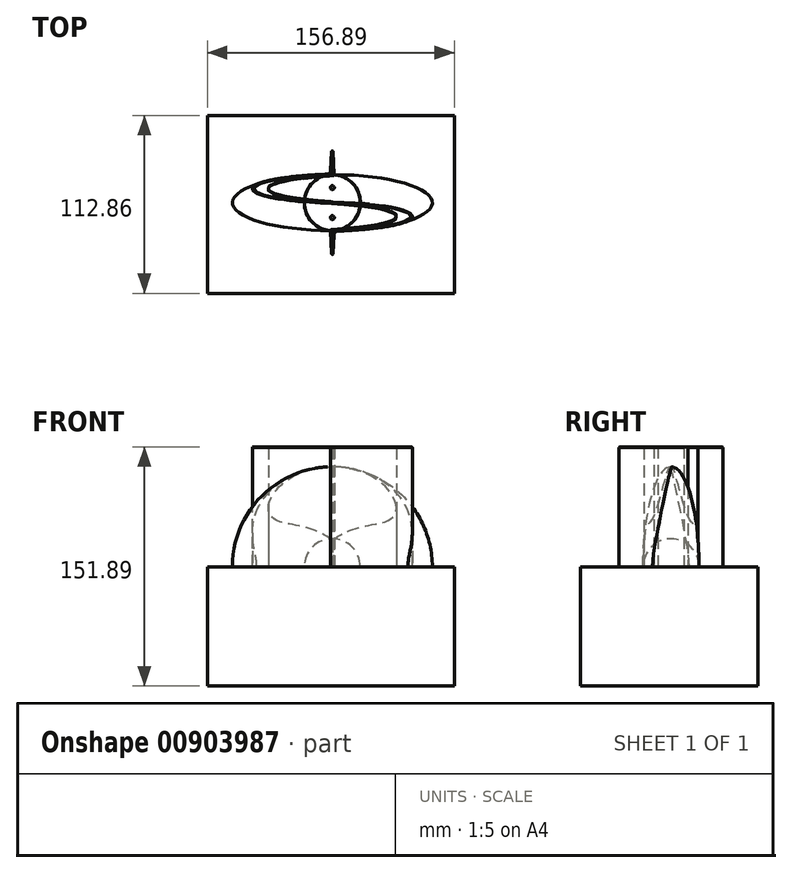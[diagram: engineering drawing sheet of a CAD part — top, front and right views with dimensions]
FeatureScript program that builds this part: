
annotation { "Feature Type Name" : "Feature", "Feature Type Description" : "" }
export const myFeature = defineFeature(function(context is Context, id is Id, definition is map)
    precondition{}
    {
        {
            var Q0;
            Q0=qCreatedBy(makeId("Top.planeOp"),FACE);
            var sketch = newSketch(context, id + "F0", { "sketchPlane" : qUnion([Q0])});
            skEllipticalArc(sketch, "E0", {});
            skEllipticalArc(sketch, "E1", {});
            skLineSegment(sketch, "E2", {"start": v(0, 0.5) * mm, "end": v(0, -0.5) * mm});
            skLineSegment(sketch, "E3", {"start": v(0, 18.17) * mm, "end": v(0, 17.17) * mm});
            const initialGuessF0  = {"E0": [0.0127, 0.008834129127051515, -1, 0, 0.0635, 0.009525, 4.9137469011750206, 1.369438406004566], "E1": [0.0381, 0.008834129127051515, -1, 0, 0.07874, 0.009525, 5.217461570130556, 1.0657237370490302]};
            skSetInitialGuess(sketch, initialGuessF0);
            skSolve(sketch);
        }
        {
            var Q0;
            Q0=qCreatedBy(makeId("Top.planeOp"),FACE);
            var sketch = newSketch(context, id + "F1", { "sketchPlane" : qUnion([Q0])});
            skLineSegment(sketch, "E4", {"start": v(-1.27, 17.17) * mm, "end": v(1.27, 17.17) * mm});
            skLineSegment(sketch, "E5", {"start": v(1.27, 17.17) * mm, "end": v(0, 42.57) * mm});
            skLineSegment(sketch, "E6", {"start": v(0, 42.57) * mm, "end": v(-1.27, 17.17) * mm});
            skSolve(sketch);
        }
        {
            var Q0;
            Q0=makeQuery(id+"F0.imprint","IMPRINT",FACE,{"disambiguationData":[TD([[makeQuery(id+"F0.imprint","IMPRINT",EDGE,{"derivedFrom":sQuery(id+"F0.wireOp",EDGE,"E0")}),1.0]])]});
            var Q1;
            Q1=makeQuery(id+"F1.imprint","IMPRINT",FACE,{"disambiguationData":[TD([[makeQuery(id+"F1.imprint","IMPRINT",EDGE,{"derivedFrom":sQuery(id+"F1.wireOp",EDGE,"E4")}),1.0]])]});
            extrude(context, id + "F2", {"entities" : qUnion([Q0, Q1]), "depth" : 76.2 * mm, "offsetDistance" : 25.4 * mm});
        }
        {
            var Q0;
            Q0=qCreatedBy(makeId("Front.planeOp"),FACE);
            var sketch = newSketch(context, id + "F3", { "sketchPlane" : qUnion([Q0])});
            skLineSegment(sketch, "E7", {"start": v(0, 85.95) * mm, "end": v(0, -92.06) * mm});
            skSolve(sketch);
        }
        {
            var Q0;
            Q0=makeQuery(id+"F2.opExtrude","SWEPT_BODY",BODY,{"disambiguationData":[OSD([sQuery(id+"F1.wireOp",EDGE,"E4"),sQuery(id+"F1.wireOp",EDGE,"E5"),sQuery(id+"F1.wireOp",EDGE,"E6")])]});
            var Q1;
            Q1=makeQuery(id+"F2.opExtrude","SWEPT_BODY",BODY,{"disambiguationData":[OSD([sQuery(id+"F0.wireOp",EDGE,"E0"),sQuery(id+"F0.wireOp",EDGE,"E1"),sQuery(id+"F0.wireOp",EDGE,"E2"),sQuery(id+"F0.wireOp",EDGE,"E3")])]});
            var Q2;
            Q2=sQuery(id+"F3.wireOp",EDGE,"E7");
            circularPattern(context, id + "F4", {"entities" : qUnion([Q0, Q1]), "axis" : qUnion([Q2]), "angle" : 360 * degree, "instanceCount" : 2, "equalSpace" : true});
        }
        {
            var Q0;
            Q0=makeQuery(id+"F2.opExtrude","SWEPT_BODY",BODY,{"disambiguationData":[OSD([sQuery(id+"F0.wireOp",EDGE,"E0"),sQuery(id+"F0.wireOp",EDGE,"E1"),sQuery(id+"F0.wireOp",EDGE,"E2"),sQuery(id+"F0.wireOp",EDGE,"E3")])]});
            var Q1;
            Q1=makeQuery(id+"F2.opExtrude","SWEPT_BODY",BODY,{"disambiguationData":[OSD([sQuery(id+"F1.wireOp",EDGE,"E4"),sQuery(id+"F1.wireOp",EDGE,"E5"),sQuery(id+"F1.wireOp",EDGE,"E6")])]});
            var Q2;
            Q2=makeQuery(id+"F4.opPattern","COPY",BODY,{"derivedFrom":makeQuery(id+"F2.opExtrude","SWEPT_BODY",BODY,{"disambiguationData":[OSD([sQuery(id+"F0.wireOp",EDGE,"E0"),sQuery(id+"F0.wireOp",EDGE,"E1"),sQuery(id+"F0.wireOp",EDGE,"E2"),sQuery(id+"F0.wireOp",EDGE,"E3")])]}),"instanceName":"1"});
            var Q3;
            Q3=makeQuery(id+"F4.opPattern","COPY",BODY,{"derivedFrom":makeQuery(id+"F2.opExtrude","SWEPT_BODY",BODY,{"disambiguationData":[OSD([sQuery(id+"F1.wireOp",EDGE,"E4"),sQuery(id+"F1.wireOp",EDGE,"E5"),sQuery(id+"F1.wireOp",EDGE,"E6")])]}),"instanceName":"1"});
            booleanBodies(context, id + "F5", {"operationType" : BooleanOperationType.UNION, "tools" : qUnion([Q0, Q1, Q2, Q3])});
        }
        {
            var Q0;
            Q0=makeQuery(id+"F2.opExtrude","SWEPT_EDGE",EDGE,{"disambiguationData":[OSD([sQuery(id+"F1.wireOp",EDGE,"E4"),sQuery(id+"F1.wireOp",EDGE,"E5")])]});
            var Q1;
            Q1=makeQuery(id+"F4.opPattern","COPY",EDGE,{"derivedFrom":makeQuery(id+"F2.opExtrude","SWEPT_EDGE",EDGE,{"disambiguationData":[OSD([sQuery(id+"F1.wireOp",EDGE,"E4"),sQuery(id+"F1.wireOp",EDGE,"E5")])]}),"instanceName":"1"});
            fillet(context, id + "F6", {"entities" : qUnion([Q0, Q1]), "radius" : 0.76 * mm, "tangentPropagation" : true, "allowEdgeOverflow" : false});
        }
        {
            var Q0;
            Q0=makeQuery(id+"F5.opBoolean","INTERSECT",EDGE,{"derivedFrom":[makeQuery(id+"F2.opExtrude","SWEPT_FACE",FACE,{"disambiguationData":[OSD([sQuery(id+"F0.wireOp",EDGE,"E0")])]}),makeQuery(id+"F2.opExtrude","SWEPT_FACE",FACE,{"disambiguationData":[OSD([sQuery(id+"F1.wireOp",EDGE,"E6")])]})]});
            var Q1;
            Q1=makeQuery(id+"F5.opBoolean","INTERSECT",EDGE,{"derivedFrom":[makeQuery(id+"F4.opPattern","COPY",FACE,{"derivedFrom":makeQuery(id+"F2.opExtrude","SWEPT_FACE",FACE,{"disambiguationData":[OSD([sQuery(id+"F0.wireOp",EDGE,"E0")])]}),"instanceName":"1"}),makeQuery(id+"F4.opPattern","COPY",FACE,{"derivedFrom":makeQuery(id+"F2.opExtrude","SWEPT_FACE",FACE,{"disambiguationData":[OSD([sQuery(id+"F1.wireOp",EDGE,"E6")])]}),"instanceName":"1"})]});
            fillet(context, id + "F7", {"entities" : qUnion([Q0, Q1]), "radius" : 2.54 * mm, "tangentPropagation" : true, "allowEdgeOverflow" : false});
        }
        {
            var Q0;
            Q0=makeQuery(id+"F2.opExtrude","SWEPT_EDGE",EDGE,{"disambiguationData":[OSD([sQuery(id+"F1.wireOp",EDGE,"E5"),sQuery(id+"F1.wireOp",EDGE,"E6")])]});
            var Q1;
            Q1=makeQuery(id+"F4.opPattern","COPY",EDGE,{"derivedFrom":makeQuery(id+"F2.opExtrude","SWEPT_EDGE",EDGE,{"disambiguationData":[OSD([sQuery(id+"F1.wireOp",EDGE,"E5"),sQuery(id+"F1.wireOp",EDGE,"E6")])]}),"instanceName":"1"});
            fillet(context, id + "F8", {"entities" : qUnion([Q0, Q1]), "radius" : 0.5 * mm, "tangentPropagation" : true, "allowEdgeOverflow" : false});
        }
        {
            var Q0;
            {var subQ0=sQuery(id+"F0.wireOp",EDGE,"E2");Q0=makeQuery(id+"F5.opBoolean","MERGE",EDGE,{"derivedFrom":[makeQuery(id+"F2.opExtrude","SWEPT_EDGE",EDGE,{"disambiguationData":[OSD([sQuery(id+"F0.wireOp",EDGE,"E1"),subQ0])]}),makeQuery(id+"F4.opPattern","COPY",EDGE,{"derivedFrom":makeQuery(id+"F2.opExtrude","SWEPT_EDGE",EDGE,{"disambiguationData":[OSD([sQuery(id+"F0.wireOp",EDGE,"E0"),subQ0])]}),"instanceName":"1"})]});}
            var Q1;
            {var subQ0=sQuery(id+"F0.wireOp",EDGE,"E2");Q1=makeQuery(id+"F5.opBoolean","MERGE",EDGE,{"derivedFrom":[makeQuery(id+"F2.opExtrude","SWEPT_EDGE",EDGE,{"disambiguationData":[OSD([sQuery(id+"F0.wireOp",EDGE,"E0"),subQ0])]}),makeQuery(id+"F4.opPattern","COPY",EDGE,{"derivedFrom":makeQuery(id+"F2.opExtrude","SWEPT_EDGE",EDGE,{"disambiguationData":[OSD([sQuery(id+"F0.wireOp",EDGE,"E1"),subQ0])]}),"instanceName":"1"})]});}
            fillet(context, id + "F9", {"entities" : qUnion([Q0, Q1]), "radius" : 25.4 * mm, "tangentPropagation" : true, "allowEdgeOverflow" : false});
        }
        {
            var Q0;
            Q0=makeQuery(id+"F4.opPattern","COPY",EDGE,{"derivedFrom":makeQuery(id+"F2.opExtrude","CAP_EDGE",EDGE,{"disambiguationData":[OSD([sQuery(id+"F0.wireOp",EDGE,"E1")])],"isStart":false}),"instanceName":"1"});
            var Q1;
            Q1=makeQuery(id+"F4.opPattern","COPY",EDGE,{"derivedFrom":makeQuery(id+"F2.opExtrude","CAP_EDGE",EDGE,{"disambiguationData":[OSD([sQuery(id+"F0.wireOp",EDGE,"E0")])],"isStart":false}),"instanceName":"1"});
            chamfer(context, id + "F10", {"entities" : qUnion([Q0, Q1]), "width" : 0.46 * mm, "tangentPropagation" : true});
        }
        {
            var Q0;
            Q0=qCreatedBy(makeId("Top.planeOp"),FACE);
            var sketch = newSketch(context, id + "F11", { "sketchPlane" : qUnion([Q0])});
            skArc(sketch, "E8", {"start": v(0, 17.78) * mm, "mid": v(-17.78, 0) * mm, "end": v(0, -17.78) * mm});
            skLineSegment(sketch, "E9", {"start": v(0, 17.78) * mm, "end": v(0, -17.78) * mm});
            skSolve(sketch);
        }
        {
            var Q0;
            Q0 = qSketchRegion(id + "F11", true);
            var Q1;
            Q1=sQuery(id+"F11.wireOp",EDGE,"E9");
            revolve(context, id + "F12", {"surfaceOperationType" : NewSurfaceOperationType.NEW, "entities" : qUnion([Q0]), "axis" : qUnion([Q1]), "revolveType" : RevolveType.ONE_DIRECTION, "oppositeDirection" : true, "angle" : 180 * degree});
        }
        {
            var Q0;
            Q0=qCreatedBy(makeId("Top.planeOp"),FACE);
            var sketch = newSketch(context, id + "F13", { "sketchPlane" : qUnion([Q0])});
            skEllipticalArc(sketch, "E10", {});
            skLineSegment(sketch, "E11", {"start": v(0, 17.78) * mm, "end": v(0, -17.78) * mm});
            const initialGuessF13  = {"E10": [0, 0, -1, 0, 0.0635, 0.01778, 4.71238898038469, 1.5707963267948966]};
            skSetInitialGuess(sketch, initialGuessF13);
            skSolve(sketch);
        }
        {
            var Q0;
            Q0=makeQuery(id+"F13.imprint","IMPRINT",FACE,{"disambiguationData":[TD([[makeQuery(id+"F13.imprint","IMPRINT",EDGE,{"derivedFrom":sQuery(id+"F13.wireOp",EDGE,"E10")}),1.0]])]});
            var Q1;
            Q1=sQuery(id+"F13.wireOp",EDGE,"E11");
            revolve(context, id + "F14", {"surfaceOperationType" : NewSurfaceOperationType.NEW, "entities" : qUnion([Q0]), "axis" : qUnion([Q1]), "revolveType" : RevolveType.ONE_DIRECTION, "oppositeDirection" : true, "angle" : 180 * degree});
        }
        {
            var Q0;
            Q0=makeQuery(id+"F2.opExtrude","SWEPT_BODY",BODY,{"disambiguationData":[OSD([sQuery(id+"F0.wireOp",EDGE,"E0"),sQuery(id+"F0.wireOp",EDGE,"E1"),sQuery(id+"F0.wireOp",EDGE,"E2"),sQuery(id+"F0.wireOp",EDGE,"E3")])]});
            var Q1;
            Q1=makeQuery(id+"F14.opRevolve","SWEPT_BODY",BODY,{"disambiguationData":[OSD([sQuery(id+"F13.wireOp",EDGE,"E10"),sQuery(id+"F13.wireOp",EDGE,"E11")])]});
            booleanBodies(context, id + "F15", {"operationType" : BooleanOperationType.SUBTRACTION, "tools" : qUnion([Q0]), "targets" : qUnion([Q1]), "keepTools" : true});
        }
        {
            var Q0;
            Q0=qCreatedBy(makeId("Top.planeOp"),FACE);
            var sketch = newSketch(context, id + "F16", { "sketchPlane" : qUnion([Q0])});
            skLineSegment(sketch, "E12.bottom", {"start": v(77.54, 55.28) * mm, "end": v(-79.35, 55.28) * mm});
            skLineSegment(sketch, "E12.top", {"start": v(77.54, -57.58) * mm, "end": v(-79.35, -57.58) * mm});
            skLineSegment(sketch, "E12.left", {"start": v(77.54, 55.28) * mm, "end": v(77.54, -57.58) * mm});
            skLineSegment(sketch, "E12.right", {"start": v(-79.35, 55.28) * mm, "end": v(-79.35, -57.58) * mm});
            skSolve(sketch);
        }
        {
            var Q0;
            Q0=makeQuery(id+"F16.imprint","IMPRINT",FACE,{"disambiguationData":[TD([[makeQuery(id+"F16.imprint","IMPRINT",EDGE,{"derivedFrom":sQuery(id+"F16.wireOp",EDGE,"E12.bottom")}),1.0]])]});
            extrude(context, id + "F17", {"entities" : qUnion([Q0]), "oppositeDirection" : true, "depth" : 75.7 * mm, "offsetDistance" : 25.4 * mm});
        }
        {
            var Q0;
            Q0=qCreatedBy(makeId("Top.planeOp"),FACE);
            var sketch = newSketch(context, id + "F18", { "sketchPlane" : qUnion([Q0])});
            skCircle(sketch, "E13", {"center": v(0, -9.53) * mm, "radius": 1.27 * mm});
            skCircle(sketch, "E14.MirrorC", {"center": v(0, 9.53) * mm, "radius": 1.27 * mm});
            skSolve(sketch);
        }
        {
            var Q0;
            Q0 = qSketchRegion(id + "F18", true);
            extrude(context, id + "F19", {"entities" : qUnion([Q0]), "depth" : 76.2 * mm, "offsetDistance" : 25.4 * mm});
        }
    });
